# Revit family: WTC-GW15W-RU30
name_source: partatom
category: HLS-Bauteile
revit_build: Autodesk Revit 2017 (Build: 20160225_1515(x64)
units: mm (PartAtom-declared; Revit-internal decimal feet)

## family parameters
Arbeitsebenenbasiert = Nein
Beim Laden mit Abzugskörper schneiden = Nein
Bemaßung runder Anschluss = Durchmesser verwenden
Gemeinsam genutzt = Nein
Immer vertikal = Ja
Raumberechnungspunkt = Nein
Teiletyp = Normal

## types (1)
- Thermo Condens, WTC-GW 15-B Ausf. W, 13.7 kW
    Anordnung, Lage = nebenstehend
    Ausstattung = Anschluss rechts
    Baugruppenkennzeichen = ????
    Beschreibung = Weishaupt Gas-Brennwertgerät WTC-GW 15-B Ausf. W
    Bestellnummer = 48301201
    Brennstoffart = gasförmige Brennstoffe
    Datanorm Nummer = 48301201
    Generiert am = 06.02.2018
    Generiert durch = Rubicon Professional Solutions GmbH
    Hersteller = MAX WEISHAUPT GMBH
    Herstellerkurzname = Weishaupt
    Modell = Thermo Condens WTC-GW 15-B Ausf. W
    Name der Richtlinie = Wärmeerzeuger
    Produktgruppe = Brennwert-Kessel
    Quelle = http://www.vdi3805-portal.de
    Revisionsdatum der VDI-Datei = 09.10.2017
    Stand der Richtlinie = 01.06.2004
    TGA-Nr = 002001000004000000001000000004002000???00000000012???00001?????0000100000000000000000001
    Trinkwasserprinzip = Speicher extern
    Typenbezeichnung (Name) = Thermo Condens, WTC-GW 15-B Ausf. W, 13.7 kW
    Typenkommentare = Die Daten geben den Stand des eingeblendeten Datums wieder. Fuer Vollstaendigkeit und Richtigkeit kann keine Gewaehr uebernommen werden!
    URL = http://www.weishaupt.de
    VDI3805-Richtlinienblatt = 3
    Web-Adresse = http://www.vdi3805-portal.de
    WebService = http://www.vdi3805-portal.de
    Werkstoff = Aluminium
    XML = <?xml version="1.0"?>
<pData xmlns="http://www.rubicon-professional.de xmlns:xsi="http://www.w3.org filename="PART03_Weishaupt.VDI" shortname="Weishaupt" manufacturername="MAX WEISHAUPT GMBH" tganr="002001000004000000001000000004002000???00000000012???00001?????0000100000000000000000001|1" language="de-DE"/><REC010 IDX="010" index="3" content="010;3;200406;MAX WEISHAUPT GMBH;20171009;http://www.weishaupt.de;Die Daten geben den Stand des eingeblendeten Datums wieder. Fuer Vollstaendigkeit und Richtigkeit kann keine Gewaehr uebernommen werden!;1234567890123;;;1;20170801;DEU;DE;201110;"><RECORDS_100><REC100 IDX="100" index="2" content="100;2;2;Wandhaengender Waermeerzeuger, fuer Heizung;;;20070412;"><RECORDS_110><REC110 IDX="110" index="1" content="110;1;1;mit Geblaese;;;20070412;"><RECORDS_200><REC200 IDX="200" index="4" content="200;4;Aluminium;"/></RECORDS_200><RECORDS_300><REC300 IDX="300" index="1" content="300;1;gasfoermige Brennstoffe;"/></RECORDS_300><RECORDS_400><REC400 IDX="400" index="4" content="400;4;Speicher extern;"><RECORDS_450><REC450 IDX="450" index="2" content="450;2;nebenstehend;"/></RECORDS_450></REC400></RECORDS_400><RECORDS_500><REC500 IDX="500" index="1" content="500;1;Anschluss rechts;"/><REC500 IDX="500" index="2" content="500;2;Anschluss links;"/></RECORDS_500><RECORDS_700><REC700 IDX="700" index="12" content="700;12;3;Thermo Condens;WTC-GW 15-B Ausf. W;13.7;41;2.2;;;;;1.9;3;Brennwert-Kessel;999;sonstige;1.17;3;raumluftabhaengig oder -unabhaengig;1;1;125;80;14;;98.2;0.004;0.076;13.7;"><RECORDS_710_01><REC71001 IDX="710.01" index="1" content="710.01;1;40/30;2.2;15.7;110.1;98.2;110.4;10;1;15;;85;;;;;;3;;76;0;;;15;24;0;7;94;7362;46;"><RECORDS_710_11><REC71011 IDX="710.11" index="1" content="710.11;1;1;3;Erdgas E;"/><REC71011 IDX="710.11" index="2" content="710.11;2;1;2;Erdgas LL;"/><REC71011 IDX="710.11" index="3" content="710.11;3;1;4;Propan;"/><REC71011 IDX="710.11" index="4" content="710.11;4;1;5;Butan;"/></RECORDS_710_11></REC71001></RECORDS_710_01><RECORDS_710_02><REC71002 IDX="710.02" index="1" content="710.02;1;10;;195;1.2;"/><REC71002 IDX="710.02" index="2" content="710.02;2;15;;90;0.8;"/><REC71002 IDX="710.02" index="3" content="710.02;3;20;;55;0.6;"/></RECORDS_710_02><RECORDS_710_03><REC71003 IDX="710.03" index="1" content="710.03;1;EG-Baumusterpruefung;CE-0085 CR 0407;"/></RECORDS_710_03><RECORDS_710_04><REC71004 IDX="710.04" index="1" content="710.04;1;;;10;0.75;"/></RECORDS_710_04><RECORDS_710_05><REC71005 IDX="710.05" index="1" content="710.05;1;5;modulierend;0.0064;;0.0009;61;53;30;8.9;8.9;28;15;17;;;;;Strahlungsbrenner mit Fecralloy-Oberflaeche;;14;"/></RECORDS_710_05><RECORDS_710_10><REC71010 IDX="710.10" index="1" content="710.10;1;2;335;520;792;Geraetemass;"/></RECORDS_710_10><RECORDS_710_12><REC71012 IDX="710.12" index="1" content="710.12;1;6;Aussenfuehler mit modulierendem Volumenstrom;4;1;1;0;1;1;24;0;1;1;1;1;1;Weishaupt Energie Manager WEM;;4;0;"/></RECORDS_710_12><RECORDS_720><REC720 IDX="720" index="1" content="720;1;48301201;"/><REC720 IDX="720" index="2" content="720;2;48301200;"/></RECORDS_720><RECORDS_740><REC740 IDX="740" index="6" content="740;6;ErP;811/2013/EU;"/><REC740 IDX="740" index="5" content="740;5;EN ISO;9614-2:1996;"/><REC740 IDX="740" index="4" content="740;4;EN;15502-2-1:2013;"/><REC740 IDX="740" index="3" content="740;3;EN;15502-1:2015;"/><REC740 IDX="740" index="2" content="740;2;EDD;2014/C207/02;"/><REC740 IDX="740" index="1" content="740;1;CE-Nr.;0085 CR 0407;"/></RECORDS_740><RECORDS_760><REC760 IDX="760" index="1" content="760;1;Hydraulik-Zubehoer Heizung;"/><REC760 IDX="760" index="2" content="760;2;Hydraulik-Zubehoer Trinkwasser;"/><REC760 IDX="760" index="3" content="760;3;Gasanschluss-Zubehoer;"/><REC760 IDX="760" index="7" content="760;7;Energiespeicher;"/><REC760 IDX="760" index="8" content="760;8;Trinkwasserspeicher;"/></RECORDS_760></REC700></RECORDS_700></REC110></RECORDS_110></REC100></RECORDS_100><RECORDS_970><REC970 IDX="970" index="100" content="970;100;WTC-GW 15/25-B (RFER);0;QUAD;0;0;0;1;0;0;0;1;0;1;1;1;0;0;0;0;0;0;0;0;"><RECORDS_970_02><REC97002 IDX="970.02" index="1" content="970.02;1;G;QUAD;-260;0;0;1;0;0;0;1;0;520;-335;792;0;0;0;0;0;0;0;1;"/><REC97002 IDX="970.02" index="20" content="970.02;20;G;ZYLI;120;-50;0;0;0;-1;0;1;0;40;9;0;0;0;0;0;0;0;0;11;"/><REC97002 IDX="970.02" index="21" content="970.02;21;G;ZYLI;-120;-50;0;0;0;-1;0;1;0;40;9;0;0;0;0;0;0;0;0;10;"/><REC97002 IDX="970.02" index="25" content="970.02;25;G;ZYLI;0;-50;0;0;0;-1;0;1;0;40;10;0;0;0;0;0;0;0;0;12;"/><REC97002 IDX="970.02" index="26" content="970.02;26;G;ZYLI;-210;-99.2;0;0;0;-1;0;1;0;20;11;0;0;0;0;0;0;0;0;3;"/><REC97002 IDX="970.02" index="41" content="970.02;41;G;RURO;0;-142;770;0;0;1;0;1;0;1;50;40;0;0;0;0;0;0;0;4;"/></RECORDS_970_02><RECORDS_970_03><REC97003 IDX="970.03" index="1" content="970.03;1;G;TRAN;0;-335;0;1;0;0;0;1;0;0;0;1;792;100;0;0;0;0;0;1;"/><REC97003 IDX="970.03" index="2" content="970.03;2;G;TRAN;0;-335;0;1;0;0;0;1;0;0;0;1;792;120;0;0;0;0;0;4;"/><REC97003 IDX="970.03" index="3" content="970.03;3;G;TRAN;0;-330;789;1;0;0;0;1;0;0;0;1;2;400;0;0;0;0;0;1;"/><REC97003 IDX="970.03" index="4" content="970.03;4;G;TRAN;0;-330;789;1;0;0;0;1;0;0;0;1;2;450;0;0;0;0;0;1;350;"/><REC97003 IDX="970.03" index="5" content="970.03;5;G;TRAN;0;-335;789;1;0;0;0;1;0;0;0;1;2;480;0;0;0;0;0;1;350;"/><REC97003 IDX="970.03" index="10" content="970.03;10;G;QUAD;260;0;0;-1;0;0;0;-1;0;5;319.5;792;0;0;0;0;0;0;0;1;"/><REC97003 IDX="970.03" index="11" content="970.03;11;G;QUAD;-260;0;0;0;-1;0;1;0;0;124.5;5;792;0;0;0;0;0;0;0;1;"/><REC97003 IDX="970.03" index="12" content="970.03;12;G;QUAD;-150;0;740;1;0;0;0;1;0;270;-300;20;0;0;0;0;0;0;0;4;"/><REC97003 IDX="970.03" index="15" content="970.03;15;G;QUAD;-185;0;120;1;0;0;0;1;0;305;-300;620;0;0;0;0;0;0;0;4;"/><REC97003 IDX="970.03" index="16" content="970.03;16;G;QUAD;101;-331;0;-1;0;0;0;-1;0;6;1;792;0;0;0;0;0;0;0;100;"/><REC97003 IDX="970.03" index="30" content="970.03;30;G;RURO;0;-142;760;0;0;1;0;1;0;2.5;22;65;0;0;0;0;0;0;0;4;"/><REC97003 IDX="970.03" index="31" content="970.03;31;G;RURO;0;-142;770;0;0;1;0;1;0;1;50;40;0;0;0;0;0;0;0;4;"/><REC97003 IDX="970.03" index="32" content="970.03;32;G;RURR;0;-142;800;0;0;1;0;1;0;2;5;42;42;50;0;0;0;0;0;4;"/><REC97003 IDX="970.03" index="35" content="970.03;35;G;ZYLI;-155;-142;782;0;0;1;0;1;0;30;15;0;0;0;0;0;0;0;0;5;"/><REC97003 IDX="970.03" index="36" content="970.03;36;G;ROTA;-155;-142;792;1;0;0;0;0;1;0;1;0;0;0;0;360;200;0;0;3;"/><REC97003 IDX="970.03" index="37" content="970.03;37;G;VKNT;-155;-142;812;0;0;1;0;1;0;10;15;25;0;0;0;0;0;0;0;5;"/><REC97003 IDX="970.03" index="38" content="970.03;38;G;ZYLI;-155;-142;822;0;0;1;0;1;0;5;15;0;0;0;0;0;0;0;0;5;"/><REC97003 IDX="970.03" index="39" content="970.03;39;G;ROTA;-95;-142;792;1;0;0;0;0;1;0;1;0;0;0;0;360;200;0;0;3;"/><REC97003 IDX="970.03" index="40" content="970.03;40;G;ZYLI;-95;-142;792;0;0;1;-1;0;0;2;15.5;0;0;0;0;0;0;0;0;3;"/><REC97003 IDX="970.03" index="44" content="970.03;44;G;RURO;-155;-142;827;0;0;1;0;1;0;3;20;20;0;0;0;0;0;0;0;5;"/><REC97003 IDX="970.03" index="1401" content="970.03;1401;G;ZYLI;-155;-142;827;0;0;1;0;1;0;18;17;0;0;0;0;0;0;0;0;5;"/><REC97003 IDX="970.03" index="1402" content="970.03;1402;G;ZYLI;-165;-142;845;0;0;1;0;1;0;6;4;0;0;0;0;0;0;0;0;5;"/><REC97003 IDX="970.03" index="1403" content="970.03;1403;G;VKNT;-165;-142;851;0;0;1;0;1;0;8;6;24;0;0;0;0;0;0;0;3;"/><REC97003 IDX="970.03" index="1404" content="970.03;1404;G;TOBO;-205;-143.6396103;732;0;0;1;1;0;0;90;25;12;0;0;0;0;0;0;0;3;"/><REC97003 IDX="970.03" index="45" content="970.03;45;G;TOBO;-155;-142;782;0;0;-1;-1;0;0;90;25;12;0;0;0;0;0;0;0;3;"/><REC97003 IDX="970.03" index="46" content="970.03;46;G;ZYLI;-205;-143.6396103;702;0;0;1;0;-1;0;30;12;0;0;0;0;0;0;0;0;3;"/><REC97003 IDX="970.03" index="48" content="970.03;48;G;ZYLI;-205;-143.6396103;511.06601718;0;0;1;0;-1;0;190.9339822;9.5;0;0;0;0;0;0;0;0;5;"/><REC97003 IDX="970.03" index="49" content="970.03;49;G;TOBO;-205;-139.24621202;500.45941546;0;-0.707107;0.707107;0;0.707107;0.707107;45;15;9.5;0;0;0;0;0;0;0;5;"/><REC97003 IDX="970.03" index="50" content="970.03;50;G;ZYLI;-205;-54.3934;415.60660172;0;-0.707107;0.707107;0;0.707107;0.707107;120;9.5;0;0;0;0;0;0;0;0;5;"/><REC97003 IDX="970.03" index="51" content="970.03;51;G;TOBO;-205;-50;405;0;0;1;0;-1;0;45;15;9.5;0;0;0;0;0;0;0;5;"/><REC97003 IDX="970.03" index="52" content="970.03;52;G;ZYLI;-205;-50;65;0;0;1;-1;0;0;340;9.5;0;0;0;0;0;0;0;0;5;"/><REC97003 IDX="970.03" index="53" content="970.03;53;G;TOBO;-205;-50;65;0;0;-1;1;0;0;90;15;9.5;0;0;0;0;0;0;0;5;"/><REC97003 IDX="970.03" index="54" content="970.03;54;G;ZYLI;-190;-50;50;1;0;0;0;0;-1;55;9.5;0;0;0;0;0;0;0;0;5;"/><REC97003 IDX="970.03" index="55" content="970.03;55;G;RURB;-135;-50;50;1;0;0;0;0;-1;2;90;15;9.5;9.5;0;0;0;0;0;5;"/><REC97003 IDX="970.03" index="56" content="970.03;56;G;RURO;-120;-50;35;0;0;-1;0;1;0;2;75;9.5;0;0;0;0;0;0;0;5;"/><REC97003 IDX="970.03" index="60" content="970.03;60;G;ZYLI;120.35534;-150;157.78174593;1;0;0;0;0;-1;50;9.5;0;0;0;0;0;0;0;0;5;"/><REC97003 IDX="970.03" index="61" content="970.03;61;G;TOBO;170.35533905;-150;157.78174593;1;0;0;0;1;0;90;15;9.5;0;0;0;0;0;0;0;5;"/><REC97003 IDX="970.03" index="62" content="970.03;62;G;ZYLI;185.35533905;-135;157.78174593;0;1;0;1;0;0;70;9.5;0;0;0;0;0;0;0;0;5;"/><REC97003 IDX="970.03" index="63" content="970.03;63;G;TOBO;185.35533905;-50;142.78174593;0;0;1;0;-1;0;90;15;9.5;0;0;0;0;0;0;0;5;"/><REC97003 IDX="970.03" index="64" content="970.03;64;G;ZYLI;185.35533905;-50;117.78174593;0;0;1;1;0;0;25;9.5;0;0;0;0;0;0;0;0;5;"/><REC97003 IDX="970.03" index="65" content="970.03;65;G;TOBO;180.96194077;-50;107.17514421;0.707107;0;0.707107;-0.707107;0;0.707107;45;15;9.5;0;0;0;0;0;0;0;5;"/><REC97003 IDX="970.03" index="66" content="970.03;66;G;ZYLI;124.39339828;-50;50.6066;0.707107;0;0.707107;-0.707107;0;0.707107;80;9.5;0;0;0;0;0;0;0;0;5;"/><REC97003 IDX="970.03" index="67" content="970.03;67;G;TOBO;120;-50;40;0;0;1;1;0;0;45;15;9.5;0;0;0;0;0;0;0;5;"/><REC97003 IDX="970.03" index="68" content="970.03;68;G;RURO;120;-50;40;0;0;-1;0;1;0;2;80;9.5;0;0;0;0;0;0;0;5;"/><REC97003 IDX="970.03" index="82" content="970.03;82;G;RURO;0;-50;50;0;0;-1;0;1;0;2;90;10;0;0;0;0;0;0;0;12;"/><REC97003 IDX="970.03" index="83" content="970.03;83;G;TOBO;0;-50;50;0;0;1;-0.990268;-0.139173;0;75;15;10;0;0;0;0;0;0;0;12;"/><REC97003 IDX="970.03" index="84" content="970.03;84;G;ZYLI;-11.00951765;-51.54728568;64.48888739;-0.956526;-0.134431;0.258819;0.2563;0.036021;0.965926;210;10;0;0;0;0;0;0;0;0;12;"/><REC97003 IDX="970.03" index="85" content="970.03;85;G;TOBO;-211.87988141;-79.77781859;118.84083284;-0.956526;-0.134431;0.258819;0.2563;0.036021;0.965926;75;15;10;0;0;0;0;0;0;0;12;"/><REC97003 IDX="970.03" index="86" content="970.03;86;G;ZYLI;-222.88940239;-81.32510829;133.32971727;0;0;1;-0.990268;-0.139173;0;200;10;0;0;0;0;0;0;0;0;12;"/><REC97003 IDX="970.03" index="87" content="970.03;87;G;TOBO;-222.88940239;-81.32510829;333.32971727;0;0;1;1;0.000001;0;90;15;10;0;0;0;0;0;0;0;12;"/><REC97003 IDX="970.03" index="88" content="970.03;88;G;ZYLI;-207.88940239;-81.32510829;348.32971727;1;0;0;0;0;1;20;10;0;0;0;0;0;0;0;0;12;"/><REC97003 IDX="970.03" index="90" content="970.03;90;G;RURO;-210;-99.2;60;0;0;-1;0;1;0;2;80;11;0;0;0;0;0;0;0;3;"/><REC97003 IDX="970.03" index="91" content="970.03;91;G;TOBO;-210;-99.2;60;0;0;1;1;0;0;45;15;11;0;0;0;0;0;0;0;3;"/><REC97003 IDX="970.03" index="92" content="970.03;92;G;ZYLI;-205.60660172;-99.2;70.60660172;0.7071068;0;0.7071068;-0.7071068;0;0.7071068;50;11;0;0;0;0;0;0;0;0;3;"/><REC97003 IDX="970.03" index="93" content="970.03;93;G;TOBO;-170.25126266;-99.2;105.96194078;0.707107;0;0.707107;-0.707107;0;0.707107;45;15;11;0;0;0;0;0;0;0;3;"/><REC97003 IDX="970.03" index="94" content="970.03;94;G;ZYLI;-165.85786;-99.2;116.56854;0;0;1;1;0;0;5;11;0;0;0;0;0;0;0;0;3;"/><REC97003 IDX="970.03" index="98" content="970.03;98;G;RURO;-120;-50;0;0;0;-1;0;1;0;1;10;10;0;0;0;0;0;0;0;10;"/><REC97003 IDX="970.03" index="99" content="970.03;99;G;RURO;120;-50;0;0;0;-1;0;1;0;1;10;10;0;0;0;0;0;0;0;11;"/><REC97003 IDX="970.03" index="100" content="970.03;100;D;STRE;0;0;0;1;0;0;0;1;0;101;-260;210;-260;5;0;0;0;0;0;0;"/><REC97003 IDX="970.03" index="101" content="970.03;101;D;BOGN;0;0;0;1;0;0;0;1;0;102;-260;5;-255;0;5;-255;5;0;0;0;"/><REC97003 IDX="970.03" index="102" content="970.03;102;D;STRE;0;0;0;1;0;0;0;1;0;103;-255;0;95;0;0;0;0;0;0;0;"/><REC97003 IDX="970.03" index="103" content="970.03;103;D;STRE;0;0;0;1;0;0;0;1;0;104;95;0;95;10;0;0;0;0;0;0;"/><REC97003 IDX="970.03" index="104" content="970.03;104;D;STRE;0;0;0;1;0;0;0;1;0;105;95;10;-255;10;0;0;0;0;0;0;"/><REC97003 IDX="970.03" index="105" content="970.03;105;D;STRE;0;0;0;1;0;0;0;1;0;106;-255;10;-255;210;0;0;0;0;0;0;"/><REC97003 IDX="970.03" index="106" content="970.03;106;D;STRE;0;0;0;1;0;0;0;1;0;100;-255;210;-260;210;0;0;0;0;0;0;"/><REC97003 IDX="970.03" index="120" content="970.03;120;D;STRE;0;0;0;1;0;0;0;1;0;121;101;0;254;0;0;0;0;0;0;0;"/><REC97003 IDX="970.03" index="121" content="970.03;121;D;BOGN;0;0;0;1;0;0;0;1;0;122;254;0;260;6;6;254;6;0;0;0;"/><REC97003 IDX="970.03" index="122" content="970.03;122;D;STRE;0;0;0;1;0;0;0;1;0;123;260;6;260;15;0;0;0;0;0;0;"/><REC97003 IDX="970.03" index="123" content="970.03;123;D;STRE;0;0;0;1;0;0;0;1;0;124;260;15;258;15;0;0;0;0;0;0;"/><REC97003 IDX="970.03" index="124" content="970.03;124;D;STRE;0;0;0;1;0;0;0;1;0;125;258;15;258;6;0;0;0;0;0;0;"/><REC97003 IDX="970.03" index="125" content="970.03;125;D;BOGN;0;0;0;1;0;0;0;1;0;126;254;2;258;6;4;254;6;0;0;0;"/><REC97003 IDX="970.03" index="126" content="970.03;126;D;STRE;0;0;0;1;0;0;0;1;0;127;254;2;103;2;0;0;0;0;0;0;"/><REC97003 IDX="970.03" index="127" content="970.03;127;D;STRE;0;0;0;1;0;0;0;1;0;128;103;2;103;6;0;0;0;0;0;0;"/><REC97003 IDX="970.03" index="128" content="970.03;128;D;STRE;0;0;0;1;0;0;0;1;0;129;103;6;95;6;0;0;0;0;0;0;"/><REC97003 IDX="970.03" index="129" content="970.03;129;D;STRE;0;0;0;1;0;0;0;1;0;130;95;6;95;4;0;0;0;0;0;0;"/><REC97003 IDX="970.03" index="130" content="970.03;130;D;STRE;0;0;0;1;0;0;0;1;0;131;95;4;101;4;0;0;0;0;0;0;"/><REC97003 IDX="970.03" index="131" content="970.03;131;D;STRE;0;0;0;1;0;0;0;1;0;120;101;4;101;0;0;0;0;0;0;0;"/><REC97003 IDX="970.03" index="200" content="970.03;200;D;STRE;0;0;0;1;0;0;0;1;0;201;-16;4;-22;4;0;0;0;0;0;0;"/><REC97003 IDX="970.03" index="201" content="970.03;201;D;BOGN;0;0;0;1;0;0;0;1;0;202;-22;4;-26;0;4;-22;0;0;0;0;"/><REC97003 IDX="970.03" index="202" content="970.03;202;D;STRE;0;0;0;1;0;0;0;1;0;203;-26;0;-16;0;0;0;0;0;0;0;"/><REC97003 IDX="970.03" index="203" content="970.03;203;D;STRE;0;0;0;1;0;0;0;1;0;200;-16;0;-16;4;0;0;0;0;0;0;"/><REC97003 IDX="970.03" index="350" content="970.03;350;H;ZYLI;0;-142;770;0;0;1;0;1;0;30;62.5;0;0;0;0;0;0;0;0;0;"/><REC97003 IDX="970.03" index="400" content="970.03;400;D;STRE;0;0;0;1;0;0;0;1;0;401;-255;0;95;0;0;0;0;0;0;0;"/><REC97003 IDX="970.03" index="401" content="970.03;401;D;STRE;0;0;0;1;0;0;0;1;0;402;95;0;95;20;0;0;0;0;0;0;"/><REC97003 IDX="970.03" index="402" content="970.03;402;D;STRE;0;0;0;1;0;0;0;1;0;403;95;20;-255;205;0;0;0;0;0;0;"/><REC97003 IDX="970.03" index="403" content="970.03;403;D;STRE;0;0;0;1;0;0;0;1;0;400;-255;205;-255;0;0;0;0;0;0;0;"/><REC97003 IDX="970.03" index="450" content="970.03;450;D;STRE;0;0;0;1;0;0;0;1;0;451;95.5;20;245;20;0;0;0;0;0;0;"/><REC97003 IDX="970.03" index="451" content="970.03;451;D;STRE;0;0;0;1;0;0;0;1;0;452;245;20;250;70;0;0;0;0;0;0;"/><REC97003 IDX="970.03" index="452" content="970.03;452;D;STRE;0;0;0;1;0;0;0;1;0;453;250;70;255;70;0;0;0;0;0;0;"/><REC97003 IDX="970.03" index="453" content="970.03;453;D;STRE;0;0;0;1;0;0;0;1;0;454;255;70;255;320;0;0;0;0;0;0;"/><REC97003 IDX="970.03" index="454" content="970.03;454;D;STRE;0;0;0;1;0;0;0;1;0;455;255;320;-255;320;0;0;0;0;0;0;"/><REC97003 IDX="970.03" index="455" content="970.03;455;D;STRE;0;0;0;1;0;0;0;1;0;456;-255;320;-255;205.5;0;0;0;0;0;0;"/><REC97003 IDX="970.03" index="456" content="970.03;456;D;STRE;0;0;0;1;0;0;0;1;0;450;-255;205.5;95.5;20;0;0;0;0;0;0;"/><REC97003 IDX="970.03" index="480" content="970.03;480;D;STRE;0;0;0;1;0;0;0;1;0;481;255;74.5;250.5;74.5;0;0;0;0;0;0;"/><REC97003 IDX="970.03" index="481" content="970.03;481;D;STRE;0;0;0;1;0;0;0;1;0;482;250.5;74.5;245.5;24.5;0;0;0;0;0;0;"/><REC97003 IDX="970.03" index="482" content="970.03;482;D;STRE;0;0;0;1;0;0;0;1;0;483;245.5;24.5;95.5;24.5;0;0;0;0;0;0;"/><REC97003 IDX="970.03" index="483" content="970.03;483;D;STRE;0;0;0;1;0;0;0;1;0;484;95.5;24.5;95.5;6.5;0;0;0;0;0;0;"/><REC97003 IDX="970.03" index="484" content="970.03;484;D;STRE;0;0;0;1;0;0;0;1;0;485;95.5;6.5;103.5;6.5;0;0;0;0;0;0;"/><REC97003 IDX="970.03" index="485" content="970.03;485;D;STRE;0;0;0;1;0;0;0;1;0;486;103.5;6.5;103.5;2.5;0;0;0;0;0;0;"/><REC97003 IDX="970.03" index="486" content="970.03;486;D;STRE;0;0;0;1;0;0;0;1;0;487;103.5;2.5;254;2.5;0;0;0;0;0;0;"/><REC97003 IDX="970.03" index="487" content="970.03;487;D;BOGN;0;0;0;1;0;0;0;1;0;488;254;2.5;257.5;6;3.5;254;6;0;0;0;"/><REC97003 IDX="970.03" index="488" content="970.03;488;D;STRE;0;0;0;1;0;0;0;1;0;489;257.5;6;257.5;14.5;0;0;0;0;0;0;"/><REC97003 IDX="970.03" index="489" content="970.03;489;D;STRE;0;0;0;1;0;0;0;1;0;490;257.5;14.5;255;14.5;0;0;0;0;0;0;"/><REC97003 IDX="970.03" index="490" content="970.03;490;D;STRE;0;0;0;1;0;0;0;1;0;480;255;14.5;255;74.5;0;0;0;0;0;0;"/></RECORDS_970_03><RECORDS_970_04><REC97004 IDX="970.04" index="1" content="970.04;1;0.867;0.871;0.831;1;0.867;0.871;0.831;1;0.867;0.871;0.831;1;64;0;0;0;1;"/><REC97004 IDX="970.04" index="3" content="970.04;3;0.5;0.5;0.4;1;0.502;0.502;0.502;1;0.6;0.6;0.2;1;64;0;0;0;1;"/><REC97004 IDX="970.04" index="4" content="970.04;4;0.8118;0.8118;0.8118;1;0.7451;0.7451;0.7451;1;0.8745;0.8745;0.8745;1;48;0;0;0;1;"/><REC97004 IDX="970.04" index="5" content="970.04;5;0.3;0.2;0.1;1;0.7412;0.5529;0;1;1;0.9;0.8;1;24;0;0;0;1;"/><REC97004 IDX="970.04" index="6" content="970.04;6;0.1;0.2;0.2;0.8;0.4;0.7;0.7;0.8;0.3;0.3;0.3;0.8;16;0;0;0;1;"/><REC97004 IDX="970.04" index="10" content="970.04;10;0.7765;0;0;1;0.7765;0;0;1;1;0;0;1;64;0;0;0;1;"/><REC97004 IDX="970.04" index="11" content="970.04;11;0;0;1;1;0;0;1;1;0;0;1;1;64;0;0;0;1;"/><REC97004 IDX="970.04" index="12" content="970.04;12;1;1;0;1;1;1;0;1;1;1;0;1;64;0;0;0;1;"/><REC97004 IDX="970.04" index="100" content="970.04;100;0;0.502;0;1;0.251;0.502;0.502;1;0;0.502;0;1;64;0;0;0;1;"/></RECORDS_970_04></REC970><REC970 IDX="970" index="2" content="970;2;logo (RFER);0;QUAD;0;0;0;1;0;0;0;1;0;1;1;1;0;0;0;0;0;0;0;0;"><RECORDS_970_02><REC97002 IDX="970.02" index="1000" content="970.02;1000;G;TEXT;-10;-10;0.5;1;0;0;0;1;0;- weishaupt -;105;15;1;0;0;0;0;0;0;2;"/></RECORDS_970_02><RECORDS_970_03><REC97003 IDX="970.03" index="1" content="970.03;1;G;QUAD;-10;-5.5;0;1;0;0;0;1;0;8;1;2;0;0;0;0;0;0;0;2;"/><REC97003 IDX="970.03" index="2" content="970.03;2;G;TRAN;0;0;0;1;0;0;0;1;0;0;0;1;2;100;0;0;0;0;0;2;"/><REC97003 IDX="970.03" index="3" content="970.03;3;G;TRAN;0;0;0;1;0;0;0;1;0;0;0;1;2;200;0;0;0;0;0;2;4;"/><REC97003 IDX="970.03" index="4" content="970.03;4;H;TRAN;0;0;-1;1;0;0;0;1;0;0;0;1;4;210;0;0;0;0;0;0;"/><REC97003 IDX="970.03" index="5" content="970.03;5;G;QUAD;23.5;-10;0;1;0;0;0;1;0;1.5;10;2;0;0;0;0;0;0;0;2;"/><REC97003 IDX="970.03" index="6" content="970.03;6;G;QUAD;23.5;1.5;0;1;0;0;0;1;0;1.5;1.5;2;0;0;0;0;0;0;0;2;"/><REC97003 IDX="970.03" index="7" content="970.03;7;G;TRAN;0;0;0;1;0;0;0;1;0;0;0;1;2;300;0;0;0;0;0;2;"/><REC97003 IDX="970.03" index="8" content="970.03;8;G;TRAN;0;0;0;1;0;0;0;1;0;0;0;1;2;400;0;0;0;0;0;2;"/><REC97003 IDX="970.03" index="9" content="970.03;9;G;TRAN;0;0;0;1;0;0;0;1;0;0;0;1;2;500;0;0;0;0;0;2;10;"/><REC97003 IDX="970.03" index="10" content="970.03;10;H;TRAN;0;0;-1;1;0;0;0;1;0;0;0;1;4;520;0;0;0;0;0;0;"/><REC97003 IDX="970.03" index="11" content="970.03;11;G;TRAN;0;0;0;1;0;0;0;1;0;0;0;1;2;600;0;0;0;0;0;2;"/><REC97003 IDX="970.03" index="12" content="970.03;12;G;TRAN;0;0;0;1;0;0;0;1;0;0;0;1;2;700;0;0;0;0;0;2;13;"/><REC97003 IDX="970.03" index="13" content="970.03;13;H;TRAN;0;0;-1;1;0;0;0;1;0;0;0;1;4;720;0;0;0;0;0;0;"/><REC97003 IDX="970.03" index="14" content="970.03;14;G;TRAN;0;0;0;1;0;0;0;1;0;0;0;1;2;800;0;0;0;0;0;2;"/><REC97003 IDX="970.03" index="15" content="970.03;15;G;QUAD;85;-5.5;0;1;0;0;0;1;0;8;1;2;0;0;0;0;0;0;0;2;"/><REC97003 IDX="970.03" index="100" content="970.03;100;D;STRE;0;0;0;1;0;0;0;1;0;101;0;0;2.5;-10;0;0;0;0;0;0;"/><REC97003 IDX="970.03" index="101" content="970.03;101;D;STRE;0;0;0;1;0;0;0;1;0;102;2.5;-10;4;-10;0;0;0;0;0;0;"/><REC97003 IDX="970.03" index="102" content="970.03;102;D;STRE;0;0;0;1;0;0;0;1;0;103;4;-10;6;-4;0;0;0;0;0;0;"/><REC97003 IDX="970.03" index="103" content="970.03;103;D;STRE;0;0;0;1;0;0;0;1;0;104;6;-4;8;-10;0;0;0;0;0;0;"/><REC97003 IDX="970.03" index="104" content="970.03;104;D;STRE;0;0;0;1;0;0;0;1;0;105;8;-10;9.5;-10;0;0;0;0;0;0;"/><REC97003 IDX="970.03" index="105" content="970.03;105;D;STRE;0;0;0;1;0;0;0;1;0;106;9.5;-10;12;0;0;0;0;0;0;0;"/><REC97003 IDX="970.03" index="106" content="970.03;106;D;STRE;0;0;0;1;0;0;0;1;0;107;12;0;10.5;0;0;0;0;0;0;0;"/><REC97003 IDX="970.03" index="107" content="970.03;107;D;STRE;0;0;0;1;0;0;0;1;0;108;10.5;0;8.75;-7;0;0;0;0;0;0;"/><REC97003 IDX="970.03" index="108" content="970.03;108;D;STRE;0;0;0;1;0;0;0;1;0;109;8.75;-7;7;0;0;0;0;0;0;0;"/><REC97003 IDX="970.03" index="109" content="970.03;109;D;STRE;0;0;0;1;0;0;0;1;0;110;7;0;5.5;0;0;0;0;0;0;0;"/><REC97003 IDX="970.03" index="110" content="970.03;110;D;STRE;0;0;0;1;0;0;0;1;0;111;5.5;0;3.5;-7;0;0;0;0;0;0;"/><REC97003 IDX="970.03" index="111" content="970.03;111;D;STRE;0;0;0;1;0;0;0;1;0;112;3.5;-7;1.5;0;0;0;0;0;0;0;"/><REC97003 IDX="970.03" index="112" content="970.03;112;D;STRE;0;0;0;1;0;0;0;1;0;100;1.5;0;0;0;0;0;0;0;0;0;"/><REC97003 IDX="970.03" index="200" content="970.03;200;D;BOGN;0;0;0;1;0;0;0;1;0;201;22;-5;21;-8;5;17;-5;0;0;0;"/><REC97003 IDX="970.03" index="201" content="970.03;201;D;STRE;0;0;0;1;0;0;0;1;0;202;22;-5;13.5;-5;0;0;0;0;0;0;"/><REC97003 IDX="970.03" index="202" content="970.03;202;D;BOGN;0;0;0;1;0;0;0;1;0;203;13.5;-5;20;-6.5;3.5;16.98849952;-4.71650207;0;0;0;"/><REC97003 IDX="970.03" index="203" content="970.03;203;D;STRE;0;0;0;1;0;0;0;1;0;200;20;-6.5;21;-8;0;0;0;0;0;0;"/><REC97003 IDX="970.03" index="210" content="970.03;210;D;STRE;0;0;0;1;0;0;0;1;0;211;14;-3.5;20;-3.5;0;0;0;0;0;0;"/><REC97003 IDX="970.03" index="211" content="970.03;211;D;BOGN;0;0;0;1;0;0;0;1;0;210;20;-3.5;14;-3.5;3.5;17;-5.30277564;0;0;0;"/><REC97003 IDX="970.03" index="300" content="970.03;300;D;BOGN;0;0;0;1;0;0;0;1;0;301;36;-2;27;-2;6;31.5;-5.96862697;0;0;0;"/><REC97003 IDX="970.03" index="301" content="970.03;301;D;BOGN;0;0;0;1;0;0;0;1;0;302;27;-2;28;-5;2.5;29.33711731;-2.88762756;0;0;0;"/><REC97003 IDX="970.03" index="302" content="970.03;302;D;BOGN;0;0;0;1;0;0;0;1;0;303;28;-5;32;-6;10;32.37325787;3.9930315;0;0;0;"/><REC97003 IDX="970.03" index="303" content="970.03;303;D;BOGN;0;0;0;1;0;0;0;1;0;304;34;-6.5;32;-6;4;32.06262256;-9.99950977;0;0;0;"/><REC97003 IDX="970.03" index="304" content="970.03;304;D;BOGN;0;0;0;1;0;0;0;1;0;305;34;-8;34;-6.5;1;33.33856217;-7.25;0;0;0;"/><REC97003 IDX="970.03" index="305" content="970.03;305;D;BOGN;0;0;0;1;0;0;0;1;0;307;28;-7;34;-8;6;31.85027817;-2.39833096;0;0;0;"/><REC97003 IDX="970.03" index="307" content="970.03;307;D;STRE;0;0;0;1;0;0;0;1;0;308;28;-7;27;-8;0;0;0;0;0;0;"/><REC97003 IDX="970.03" index="308" content="970.03;308;D;BOGN;0;0;0;1;0;0;0;1;0;309;27;-8;35.5;-8.5;6.5;31.53842617;-3.34675512;0;0;0;"/><REC97003 IDX="970.03" index="309" content="970.03;309;D;BOGN;0;0;0;1;0;0;0;1;0;310;35.5;-8.5;35.5;-6;1.9;34.0690912;-7.25;0;0;0;"/><REC97003 IDX="970.03" index="310" content="970.03;310;D;BOGN;0;0;0;1;0;0;0;1;0;311;35.5;-6;32;-5;7;31.89309041;-11.99918355;0;0;0;"/><REC97003 IDX="970.03" index="311" content="970.03;311;D;BOGN;0;0;0;1;0;0;0;1;0;312;29;-4;32;-5;7;32.65638587;1.9691576;0;0;0;"/><REC97003 IDX="970.03" index="312" content="970.03;312;D;BOGN;0;0;0;1;0;0;0;1;0;313;29;-1.8;29;-4;1.2;29.47958315;-2.9;0;0;0;"/><REC97003 IDX="970.03" index="313" content="970.03;313;D;BOGN;0;0;0;1;0;0;0;1;0;314;35;-3;29;-1.8;5;31.22441089;-6.27794553;0;0;0;"/><REC97003 IDX="970.03" index="314" content="970.03;314;D;STRE;0;0;0;1;0;0;0;1;0;300;35;-3;36;-2;0;0;0;0;0;0;"/><REC97003 IDX="970.03" index="400" content="970.03;400;D;STRE;0;0;0;1;0;0;0;1;0;401;38;5;38;-10;0;0;0;0;0;0;"/><REC97003 IDX="970.03" index="401" content="970.03;401;D;STRE;0;0;0;1;0;0;0;1;0;402;38;-10;39.5;-10;0;0;0;0;0;0;"/><REC97003 IDX="970.03" index="402" content="970.03;402;D;STRE;0;0;0;1;0;0;0;1;0;403;39.5;-10;39.5;-3.5;0;0;0;0;0;0;"/><REC97003 IDX="970.03" index="403" content="970.03;403;D;BOGN;0;0;0;1;0;0;0;1;0;404;44;-3.5;39.5;-3.5;2.5;41.75;-4.58972474;0;0;0;"/><REC97003 IDX="970.03" index="404" content="970.03;404;D;STRE;0;0;0;1;0;0;0;1;0;405;44;-3.5;44;-10;0;0;0;0;0;0;"/><REC97003 IDX="970.03" index="405" content="970.03;405;D;STRE;0;0;0;1;0;0;0;1;0;406;44;-10;45.5;-10;0;0;0;0;0;0;"/><REC97003 IDX="970.03" index="406" content="970.03;406;D;STRE;0;0;0;1;0;0;0;1;0;407;45.5;-10;45.5;-3.5;0;0;0;0;0;0;"/><REC97003 IDX="970.03" index="407" content="970.03;407;D;BOGN;0;0;0;1;0;0;0;1;0;408;45.5;-3.5;39.5;-1.5;3.8;41.83366675;-4.49899975;0;0;0;"/><REC97003 IDX="970.03" index="408" content="970.03;408;D;STRE;0;0;0;1;0;0;0;1;0;409;39.5;-1.5;39.5;5;0;0;0;0;0;0;"/><REC97003 IDX="970.03" index="409" content="970.03;409;D;STRE;0;0;0;1;0;0;0;1;0;400;39.5;5;38;5;0;0;0;0;0;0;"/><REC97003 IDX="970.03" index="500" content="970.03;500;D;BOGN;0;0;0;1;0;0;0;1;0;501;50;-5;47;-6.5;3.5;49.87386317;-8.49772633;0;0;0;"/><REC97003 IDX="970.03" index="501" content="970.03;501;D;STRE;0;0;0;1;0;0;0;1;0;502;47;-6.5;47;-7.5;0;0;0;0;0;0;"/><REC97003 IDX="970.03" index="502" content="970.03;502;D;BOGN;0;0;0;1;0;0;0;1;0;503;47;-7.5;48;-9.5;2;48.9832397;-7.75838015;0;0;0;"/><REC97003 IDX="970.03" index="503" content="970.03;503;D;BOGN;0;0;0;1;0;0;0;1;0;504;48;-9.5;54.5;-9;5.5;50.91023364;-4.8330374;0;0;0;"/><REC97003 IDX="970.03" index="504" content="970.03;504;D;STRE;0;0;0;1;0;0;0;1;0;505;54.5;-9;55;-10;0;0;0;0;0;0;"/><REC97003 IDX="970.03" index="505" content="970.03;505;D;STRE;0;0;0;1;0;0;0;1;0;506;55;-10;56.5;-10;0;0;0;0;0;0;"/><REC97003 IDX="970.03" index="506" content="970.03;506;D;BOGN;0;0;0;1;0;0;0;1;0;507;56;-8.5;56.5;-10;2;57.99284251;-8.6690525;0;0;0;"/><REC97003 IDX="970.03" index="507" content="970.03;507;D;STRE;0;0;0;1;0;0;0;1;0;508;56;-8.5;56;-3;0;0;0;0;0;0;"/><REC97003 IDX="970.03" index="508" content="970.03;508;D;BOGN;0;0;0;1;0;0;0;1;0;509;56;-3;53;0;3;53;-3;0;0;0;"/><REC97003 IDX="970.03" index="509" content="970.03;509;D;STRE;0;0;0;1;0;0;0;1;0;510;53;0;49.5;0;0;0;0;0;0;0;"/><REC97003 IDX="970.03" index="510" content="970.03;510;D;BOGN;0;0;0;1;0;0;0;1;0;511;49.5;0;47;-3.5;4;50.99446618;-3.71033298;0;0;0;"/><REC97003 IDX="970.03" index="511" content="970.03;511;D;STRE;0;0;0;1;0;0;0;1;0;512;47;-3.5;48.5;-3.5;0;0;0;0;0;0;"/><REC97003 IDX="970.03" index="512" content="970.03;512;D;BOGN;0;0;0;1;0;0;0;1;0;513;50;-1.5;48.5;-3.5;2;50.4989996;-3.4367497;0;0;0;"/><REC97003 IDX="970.03" index="513" content="970.03;513;D;STRE;0;0;0;1;0;0;0;1;0;514;50;-1.5;53;-1.5;0;0;0;0;0;0;"/><REC97003 IDX="970.03" index="514" content="970.03;514;D;BOGN;0;0;0;1;0;0;0;1;0;515;54;-4;53;-1.5;1.5;52.88587039;-2.99565184;0;0;0;"/><REC97003 IDX="970.03" index="515" content="970.03;515;D;STRE;0;0;0;1;0;0;0;1;0;500;54;-4;50;-5;0;0;0;0;0;0;"/><REC97003 IDX="970.03" index="520" content="970.03;520;D;STRE;0;0;0;1;0;0;0;1;0;521;54.5;-5.5;50;-6.5;0;0;0;0;0;0;"/><REC97003 IDX="970.03" index="521" content="970.03;521;D;BOGN;0;0;0;1;0;0;0;1;0;522;50;-6.5;50;-9;1.3;50.35707142;-7.75;0;0;0;"/><REC97003 IDX="970.03" index="522" content="970.03;522;D;BOGN;0;0;0;1;0;0;0;1;0;523;50;-9;54;-8;4;51.16862976;-5.17451905;0;0;0;"/><REC97003 IDX="970.03" index="523" content="970.03;523;D;BOGN;0;0;0;1;0;0;0;1;0;520;54;-8;54.5;-5.5;5;49.50911806;-5.80182361;0;0;0;"/><REC97003 IDX="970.03" index="600" content="970.03;600;D;STRE;0;0;0;1;0;0;0;1;0;601;58;0;58;-7;0;0;0;0;0;0;"/><REC97003 IDX="970.03" index="601" content="970.03;601;D;BOGN;0;0;0;1;0;0;0;1;0;602;58;-7;61;-10;3;61;-7;0;0;0;"/><REC97003 IDX="970.03" index="602" content="970.03;602;D;STRE;0;0;0;1;0;0;0;1;0;603;61;-10;63;-10;0;0;0;0;0;0;"/><REC97003 IDX="970.03" index="603" content="970.03;603;D;BOGN;0;0;0;1;0;0;0;1;0;604;63;-10;65;-8.5;2;63.0632503;-8.001;0;0;0;"/><REC97003 IDX="970.03" index="604" content="970.03;604;D;STRE;0;0;0;1;0;0;0;1;0;605;65;-8.5;65.5;-10;0;0;0;0;0;0;"/><REC97003 IDX="970.03" index="605" content="970.03;605;D;STRE;0;0;0;1;0;0;0;1;0;606;65.5;-10;67;-10;0;0;0;0;0;0;"/><REC97003 IDX="970.03" index="606" content="970.03;606;D;BOGN;0;0;0;1;0;0;0;1;0;607;66.5;-8.5;67;-10;2;68.49284251;-8.6690525;0;0;0;"/><REC97003 IDX="970.03" index="607" content="970.03;607;D;STRE;0;0;0;1;0;0;0;1;0;608;66.5;-8.5;66.5;0;0;0;0;0;0;0;"/><REC97003 IDX="970.03" index="608" content="970.03;608;D;STRE;0;0;0;1;0;0;0;1;0;609;66.5;0;65;0;0;0;0;0;0;0;"/><REC97003 IDX="970.03" index="609" content="970.03;609;D;STRE;0;0;0;1;0;0;0;1;0;610;65;0;65;-7;0;0;0;0;0;0;"/><REC97003 IDX="970.03" index="610" content="970.03;610;D;BOGN;0;0;0;1;0;0;0;1;0;611;63;-8.5;65;-7;2;63.0632503;-6.5010004;0;0;0;"/><REC97003 IDX="970.03" index="611" content="970.03;611;D;STRE;0;0;0;1;0;0;0;1;0;612;63;-8.5;61.5;-8.5;0;0;0;0;0;0;"/><REC97003 IDX="970.03" index="612" content="970.03;612;D;BOGN;0;0;0;1;0;0;0;1;0;613;59.5;-7;61.5;-8.5;2;61.4367497;-6.5010004;0;0;0;"/><REC97003 IDX="970.03" index="613" content="970.03;613;D;STRE;0;0;0;1;0;0;0;1;0;614;59.5;-7;59.5;0;0;0;0;0;0;0;"/><REC97003 IDX="970.03" index="614" content="970.03;614;D;STRE;0;0;0;1;0;0;0;1;0;600;59.5;0;58;0;0;0;0;0;0;0;"/><REC97003 IDX="970.03" index="700" content="970.03;700;D;STRE;0;0;0;1;0;0;0;1;0;701;68.5;0;68.5;-12;0;0;0;0;0;0;"/><REC97003 IDX="970.03" index="701" content="970.03;701;D;STRE;0;0;0;1;0;0;0;1;0;702;68.5;-12;70;-12;0;0;0;0;0;0;"/><REC97003 IDX="970.03" index="702" content="970.03;702;D;STRE;0;0;0;1;0;0;0;1;0;703;70;-12;70;-9;0;0;0;0;0;0;"/><REC97003 IDX="970.03" index="703" content="970.03;703;D;BOGN;0;0;0;1;0;0;0;1;0;704;70;-9;74.5;-9;3;72.25;-7.01568652;0;0;0;"/><REC97003 IDX="970.03" index="704" content="970.03;704;D;BOGN;0;0;0;1;0;0;0;1;0;705;74.5;-9;74.5;-1;5;71.5;-5;0;0;0;"/><REC97003 IDX="970.03" index="705" content="970.03;705;D;BOGN;0;0;0;1;0;0;0;1;0;706;74.5;-1;70;-1;3;72.25;-2.98431348;0;0;0;"/><REC97003 IDX="970.03" index="706" content="970.03;706;D;STRE;0;0;0;1;0;0;0;1;0;707;70;-1;70;0;0;0;0;0;0;0;"/><REC97003 IDX="970.03" index="707" content="970.03;707;D;STRE;0;0;0;1;0;0;0;1;0;700;70;0;68.5;0;0;0;0;0;0;0;"/><REC97003 IDX="970.03" index="720" content="970.03;720;D;BOGN;0;0;0;1;0;0;0;1;0;721;74;-2.5;71;-2.5;2.5;72.5;-4.5;0;0;0;"/><REC97003 IDX="970.03" index="721" content="970.03;721;D;BOGN;0;0;0;1;0;0;0;1;0;722;71;-2.5;71;-7.5;4;74.122499;-5;0;0;0;"/><REC97003 IDX="970.03" index="722" content="970.03;722;D;BOGN;0;0;0;1;0;0;0;1;0;723;71;-7.5;74;-7.5;2.5;72.5;-5.5;0;0;0;"/><REC97003 IDX="970.03" index="723" content="970.03;723;D;BOGN;0;0;0;1;0;0;0;1;0;720;74;-7.5;74;-2.5;4;70.877501;-5;0;0;0;"/><REC97003 IDX="970.03" index="800" content="970.03;800;D;STRE;0;0;0;1;0;0;0;1;0;801;78;-1.5;78;-8;0;0;0;0;0;0;"/><REC97003 IDX="970.03" index="801" content="970.03;801;D;BOGN;0;0;0;1;0;0;0;1;0;802;78;-8;80;-10;2;80;-8;0;0;0;"/><REC97003 IDX="970.03" index="802" content="970.03;802;D;STRE;0;0;0;1;0;0;0;1;0;803;80;-10;82;-10;0;0;0;0;0;0;"/><REC97003 IDX="970.03" index="803" content="970.03;803;D;BOGN;0;0;0;1;0;0;0;1;0;804;82;-10;83;-9;1;82;-9;0;0;0;"/><REC97003 IDX="970.03" index="804" content="970.03;804;D;STRE;0;0;0;1;0;0;0;1;0;805;83;-9;83;-7.5;0;0;0;0;0;0;"/><REC97003 IDX="970.03" index="805" content="970.03;805;D;BOGN;0;0;0;1;0;0;0;1;0;806;82;-8.5;83;-7.5;1;82;-7.5;0;0;0;"/><REC97003 IDX="970.03" index="806" content="970.03;806;D;STRE;0;0;0;1;0;0;0;1;0;807;82;-8.5;80.5;-8.5;0;0;0;0;0;0;"/><REC97003 IDX="970.03" index="807" content="970.03;807;D;BOGN;0;0;0;1;0;0;0;1;0;808;79.5;-7.5;80.5;-8.5;1;80.5;-7.5;0;0;0;"/><REC97003 IDX="970.03" index="808" content="970.03;808;D;STRE;0;0;0;1;0;0;0;1;0;809;79.5;-7.5;79.5;-1.5;0;0;0;0;0;0;"/><REC97003 IDX="970.03" index="809" content="970.03;809;D;STRE;0;0;0;1;0;0;0;1;0;810;79.5;-1.5;82;-1.5;0;0;0;0;0;0;"/><REC97003 IDX="970.03" index="810" content="970.03;810;D;STRE;0;0;0;1;0;0;0;1;0;811;82;-1.5;82;0;0;0;0;0;0;0;"/><REC97003 IDX="970.03" index="811" content="970.03;811;D;STRE;0;0;0;1;0;0;0;1;0;812;82;0;79.5;0;0;0;0;0;0;0;"/><REC97003 IDX="970.03" index="812" content="970.03;812;D;STRE;0;0;0;1;0;0;0;1;0;813;79.5;0;79.5;5;0;0;0;0;0;0;"/><REC97003 IDX="970.03" index="813" content="970.03;813;D;STRE;0;0;0;1;0;0;0;1;0;814;79.5;5;78;5;0;0;0;0;0;0;"/><REC97003 IDX="970.03" index="814" content="970.03;814;D;STRE;0;0;0;1;0;0;0;1;0;815;78;5;78;0;0;0;0;0;0;0;"/><REC97003 IDX="970.03" index="815" content="970.03;815;D;STRE;0;0;0;1;0;0;0;1;0;816;78;0;76.5;0;0;0;0;0;0;0;"/><REC97003 IDX="970.03" index="816" content="970.03;816;D;STRE;0;0;0;1;0;0;0;1;0;817;76.5;0;76.5;-1.5;0;0;0;0;0;0;"/><REC97003 IDX="970.03" index="817" content="970.03;817;D;STRE;0;0;0;1;0;0;0;1;0;800;76.5;-1.5;78;-1.5;0;0;0;0;0;0;"/></RECORDS_970_03><RECORDS_970_04><REC97004 IDX="970.04" index="2" content="970.04;2;1;0;0;1;0.671;0.145;0.141;1;1;0;0;1;64;0;0;0;1;"/></RECORDS_970_04></REC970><REC970 IDX="970" index="48301201" content="970;48301201;WTC 15/25/32-B, Ausfuehrung W (OK = 1795 mm);0;QUAD;290;-835;1003;0;1;0;-1;0;0;835;580;850;0;0;0;0;0;0;0;0;"><RECORDS_970_01><REC97001 IDX="970.01" index="1" content="970.01;1;1;A;VK;NIPP;2353;DA;18;0;15;-120;-50;963;0;0;-1;0;1;0;0;0;0;0;0;0;"/><REC97001 IDX="970.01" index="2" content="970.01;2;2;E;RK;NIPP;2353;DA;18;0;15;120;-50;963;0;0;-1;0;1;0;0;0;0;0;0;0;"/><REC97001 IDX="970.01" index="3" content="970.01;3;3;A;VS;NIPP;2353;DA;15;0;15;-60;-35;963;0;0;-1;0;1;0;0;0;0;0;0;0;"/><REC97001 IDX="970.01" index="4" content="970.01;4;4;E;EK;NIPP;2353;DA;15;0;15;60;-35;963;0;0;-1;0;1;0;0;0;0;0;0;0;"/><REC97001 IDX="970.01" index="5" content="970.01;5;5;E;GAS;NIPP;2353;DA;18;0;15;0;-50;963;0;0;-1;0;1;0;0;0;0;0;0;0;"/><REC97001 IDX="970.01" index="6" content="970.01;6;6;A;AA;NIPP;1298;DN;80;0;15;0;-142;1823;0;0;1;0;1;0;0;0;0;0;0;0;"/><REC97001 IDX="970.01" index="7" content="970.01;7;7;E;VK;NIPP;1298;DN;125;0;15;0;-142;1773;0;0;1;0;1;0;0;0;0;0;0;0;"/><REC97001 IDX="970.01" index="8" content="970.01;8;8;A;AKO;MUFF;Schlauch;DA;22;0;0;-210;-99.2;983;0;0;-1;0;1;0;0;0;0;0;0;0;"/></RECORDS_970_01><RECORDS_970_02><REC97002 IDX="970.02" index="1" content="970.02;1;G;RFER;0;0;1003;1;0;0;0;1;0;0;0;0;100;0;0;0;0;0;0;0;"/><REC97002 IDX="970.02" index="22" content="970.02;22;G;ZYLI;60;-35;1003;0;0;-1;0;1;0;40;8;0;0;0;0;0;0;0;0;5;"/><REC97002 IDX="970.02" index="23" content="970.02;23;G;ZYLI;-60;-35;1003;0;0;-1;0;1;0;40;8;0;0;0;0;0;0;0;0;5;"/><REC97002 IDX="970.02" index="90" content="970.02;90;G;RFER;130;-335;1753;1;0;0;0;0;1;0;0;0;2;0;0;0;0;0;0;0;"/></RECORDS_970_02><RECORDS_970_03><REC97003 IDX="970.03" index="3" content="970.03;3;G;TRAN;0;-330;1013;1;0;0;0;1;0;0;0;1;2;400;0;0;0;0;0;1;"/><REC97003 IDX="970.03" index="4" content="970.03;4;G;TRAN;0;-330;1013;1;0;0;0;1;0;0;0;1;2;450;0;0;0;0;0;1;300;301;302;303;304;305;"/><REC97003 IDX="970.03" index="5" content="970.03;5;G;TRAN;0;-330;1013;1;0;0;0;1;0;0;0;1;2;480;0;0;0;0;0;1;"/><REC97003 IDX="970.03" index="6" content="970.03;6;G;QUAD;150.5;-240;1013;1;0;0;0;1;0;104;230;2;0;0;0;0;0;0;0;1;"/><REC97003 IDX="970.03" index="12" content="970.03;12;G;QUAD;140;-250;1353;1;0;0;0;1;0;80;240;400;0;0;0;0;0;0;0;10;"/><REC97003 IDX="970.03" index="13" content="970.03;13;G;ZYLI;150;-80;1353;0;0;-1;0;1;0;260;8;0;0;0;0;0;0;0;0;10;"/><REC97003 IDX="970.03" index="14" content="970.03;14;G;TOBO;150;-80;1093;0;0;-1;-1;0;0;90;10;8;0;0;0;0;0;0;0;10;"/><REC97003 IDX="970.03" index="15" content="970.03;15;G;ZYLI;140;-80;1083;-1;0;0;0;0;-1;150;8;0;0;0;0;0;0;0;0;10;"/><REC97003 IDX="970.03" index="16" content="970.03;16;G;TOBO;-10;-80;1083;-1;0;0;0;0;1;90;10;8;0;0;0;0;0;0;0;10;"/><REC97003 IDX="970.03" index="17" content="970.03;17;G;ZYLI;-20;-80;1093;0;0;1;-1;0;0;30;8;0;0;0;0;0;0;0;0;10;"/><REC97003 IDX="970.03" index="22" content="970.03;22;G;RURO;60;-35;1043;0;0;-1;0;1;0;2;80;8;0;0;0;0;0;0;0;5;"/><REC97003 IDX="970.03" index="23" content="970.03;23;G;TOBO;60;-35;1043;0;0;1;0;-1;0;90;10;8;0;0;0;0;0;0;0;5;"/><REC97003 IDX="970.03" index="24" content="970.03;24;G;ZYLI;60;-45;1053;0;-1;0;0;0;1;100;8;0;0;0;0;0;0;0;0;5;"/><REC97003 IDX="970.03" index="25" content="970.03;25;G;TOBO;60;-145;1053;0;-1;0;0;0;1;90;10;8;0;0;0;0;0;0;0;5;"/><REC97003 IDX="970.03" index="26" content="970.03;26;G;ZYLI;60;-155;1063;0;0;1;0;-1;0;60;8;0;0;0;0;0;0;0;0;5;"/><REC97003 IDX="970.03" index="32" content="970.03;32;G;RURO;-60;-35;1063;0;0;-1;0;1;0;2;100;8;0;0;0;0;0;0;0;5;"/><REC97003 IDX="970.03" index="33" content="970.03;33;G;TOBO;-60;-35;1063;0;0;1;-0.994522;-0.104528;0;45;10;8;0;0;0;0;0;0;0;5;"/><REC97003 IDX="970.03" index="34" content="970.03;34;G;ZYLI;-62.91288733;-35.30615542;1070.07106781;-0.703233;-0.073913;0.707107;0.703233;0.073913;0.707107;50;8;0;0;0;0;0;0;0;0;5;"/><REC97003 IDX="970.03" index="35" content="970.03;35;G;TOBO;-98.07454783;-39.00177859;1105.42640687;-0.703233;-0.073912;0.707107;-0.703233;-0.073913;-0.707106;45;10;8;0;0;0;0;0;0;0;5;"/><REC97003 IDX="970.03" index="36" content="970.03;36;G;ZYLI;-105.10687992;-39.74090328;1108.35533906;-0.9945219;-0.104528;0;0;0;1;100;8;0;0;0;0;0;0;0;0;5;"/><REC97003 IDX="970.03" index="90" content="970.03;90;G;RFER;130;-335;1753;1;0;0;0;0;1;0;0;0;2;0;0;0;0;0;0;0;"/><REC97003 IDX="970.03" index="91" content="970.03;91;G;RFER;0;0;1003;1;0;0;0;1;0;0;0;0;100;0;0;0;0;0;0;0;"/><REC97003 IDX="970.03" index="300" content="970.03;300;H;ZYLI;120;-50;1018;0;0;-1;0;1;0;20;15;0;0;0;0;0;0;0;0;0;"/><REC97003 IDX="970.03" index="301" content="970.03;301;H;ZYLI;60;-35;1018;0;0;-1;0;1;0;20;15;0;0;0;0;0;0;0;0;0;"/><REC97003 IDX="970.03" index="302" content="970.03;302;H;ZYLI;-60;-35;1018;0;0;-1;0;1;0;20;15;0;0;0;0;0;0;0;0;0;"/><REC97003 IDX="970.03" index="303" content="970.03;303;H;ZYLI;-120;-50;1018;0;0;-1;0;1;0;20;15;0;0;0;0;0;0;0;0;0;"/><REC97003 IDX="970.03" index="304" content="970.03;304;H;ZYLI;0;-50;1018;0;0;-1;0;1;0;20;18;0;0;0;0;0;0;0;0;0;"/><REC97003 IDX="970.03" index="305" content="970.03;305;H;ZYLI;-210;-99.2;1018;0;0;-1;0;1;0;20;18;0;0;0;0;0;0;0;0;0;"/><REC97003 IDX="970.03" index="400" content="970.03;400;D;STRE;0;0;0;1;0;0;0;1;0;401;-255;0;95;0;0;0;0;0;0;0;"/><REC97003 IDX="970.03" index="401" content="970.03;401;D;STRE;0;0;0;1;0;0;0;1;0;402;95;0;95;20;0;0;0;0;0;0;"/><REC97003 IDX="970.03" index="402" content="970.03;402;D;STRE;0;0;0;1;0;0;0;1;0;403;95;20;-255;205;0;0;0;0;0;0;"/><REC97003 IDX="970.03" index="403" content="970.03;403;D;STRE;0;0;0;1;0;0;0;1;0;400;-255;205;-255;0;0;0;0;0;0;0;"/><REC97003 IDX="970.03" index="450" content="970.03;450;D;STRE;0;0;0;1;0;0;0;1;0;451;95.5;20;115;20;0;0;0;0;0;0;"/><REC97003 IDX="970.03" index="451" content="970.03;451;D;STRE;0;0;0;1;0;0;0;1;0;452;115;20;150;90;0;0;0;0;0;0;"/><REC97003 IDX="970.03" index="452" content="970.03;452;D;STRE;0;0;0;1;0;0;0;1;0;453;150;90;150;320;0;0;0;0;0;0;"/><REC97003 IDX="970.03" index="453" content="970.03;453;D;STRE;0;0;0;1;0;0;0;1;0;454;150;320;-255;320;0;0;0;0;0;0;"/><REC97003 IDX="970.03" index="454" content="970.03;454;D;STRE;0;0;0;1;0;0;0;1;0;455;-255;320;-255;205.5;0;0;0;0;0;0;"/><REC97003 IDX="970.03" index="455" content="970.03;455;D;STRE;0;0;0;1;0;0;0;1;0;450;-255;205.5;95.5;20;0;0;0;0;0;0;"/><REC97003 IDX="970.03" index="480" content="970.03;480;D;STRE;0;0;0;1;0;0;0;1;0;481;150.5;90;115.5;19.5;0;0;0;0;0;0;"/><REC97003 IDX="970.03" index="481" content="970.03;481;D;STRE;0;0;0;1;0;0;0;1;0;482;115.5;19.5;95.5;19.5;0;0;0;0;0;0;"/><REC97003 IDX="970.03" index="482" content="970.03;482;D;STRE;0;0;0;1;0;0;0;1;0;483;95.5;19.5;95.5;1.5;0;0;0;0;0;0;"/><REC97003 IDX="970.03" index="483" content="970.03;483;D;STRE;0;0;0;1;0;0;0;1;0;484;95.5;1.5;103.5;1.5;0;0;0;0;0;0;"/><REC97003 IDX="970.03" index="484" content="970.03;484;D;STRE;0;0;0;1;0;0;0;1;0;485;103.5;1.5;103.5;-2.5;0;0;0;0;0;0;"/><REC97003 IDX="970.03" index="485" content="970.03;485;D;STRE;0;0;0;1;0;0;0;1;0;486;103.5;-2.5;254;-2.5;0;0;0;0;0;0;"/><REC97003 IDX="970.03" index="486" content="970.03;486;D;BOGN;0;0;0;1;0;0;0;1;0;487;254;-2.5;257.5;1;3.5;254;1;0;0;0;"/><REC97003 IDX="970.03" index="487" content="970.03;487;D;STRE;0;0;0;1;0;0;0;1;0;488;257.5;1;257.5;90;0;0;0;0;0;0;"/><REC97003 IDX="970.03" index="488" content="970.03;488;D;STRE;0;0;0;1;0;0;0;1;0;480;257.5;90;150.5;90;0;0;0;0;0;0;"/></RECORDS_970_03><RECORDS_970_04><REC97004 IDX="970.04" index="1" content="970.04;1;0.867;0.871;0.831;1;0.867;0.871;0.831;1;0.867;0.871;0.831;1;64;0;0;0;1;"/><REC97004 IDX="970.04" index="3" content="970.04;3;0.5;0.5;0.4;1;0.502;0.502;0.502;1;0.6;0.6;0.2;1;64;0;0;0;1;"/><REC97004 IDX="970.04" index="4" content="970.04;4;0.8118;0.8118;0.8118;1;0.7451;0.7451;0.7451;1;0.8745;0.8745;0.8745;1;48;0;0;0;1;"/><REC97004 IDX="970.04" index="5" content="970.04;5;0.3;0.2;0.1;1;0.7412;0.5529;0;1;1;0.9;0.8;1;24;0;0;0;1;"/><REC97004 IDX="970.04" index="6" content="970.04;6;0.1;0.2;0.2;0.8;0.4;0.7;0.7;0.8;0.3;0.3;0.3;0.8;16;0;0;0;1;"/><REC97004 IDX="970.04" index="10" content="970.04;10;0.7765;0;0;1;0.7765;0;0;1;1;0;0;1;64;0;0;0;1;"/></RECORDS_970_04></REC970></RECORDS_970></REC010></pData>

## geometry (parser evidence)
native form markers: Sweep x2
no freeform markers — native parametric forms only
